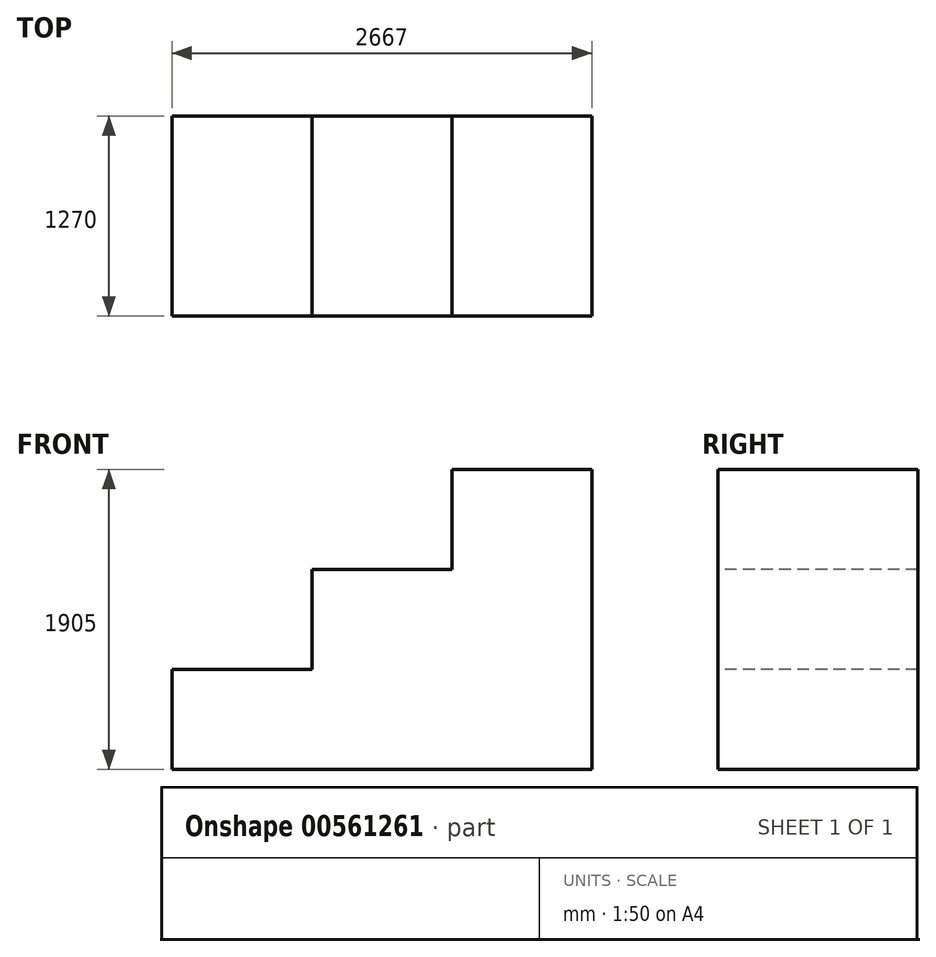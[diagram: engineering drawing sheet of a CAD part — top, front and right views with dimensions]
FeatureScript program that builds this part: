
annotation { "Feature Type Name" : "Feature", "Feature Type Description" : "" }
export const myFeature = defineFeature(function(context is Context, id is Id, definition is map)
    precondition{}
    {
        {
            var Q0;
            Q0=qCreatedBy(makeId("Front.planeOp"),FACE);
            var sketch = newSketch(context, id + "F0", { "sketchPlane" : qUnion([Q0])});
            skLineSegment(sketch, "E0.bottom", {"start": v(-1333.5, 952.5) * mm, "end": v(1333.5, 952.5) * mm});
            skLineSegment(sketch, "E0.top", {"start": v(-1333.5, -952.5) * mm, "end": v(1333.5, -952.5) * mm});
            skLineSegment(sketch, "E0.left", {"start": v(-1333.5, 952.5) * mm, "end": v(-1333.5, -952.5) * mm});
            skLineSegment(sketch, "E0.right", {"start": v(1333.5, 952.5) * mm, "end": v(1333.5, -952.5) * mm});
            skPoint(sketch, "E0.middle", {"position": v(0, 0) * mm});
            skSolve(sketch);
        }
        {
            var Q0;
            Q0 = qSketchRegion(id + "F0", true);
            extrude(context, id + "F1", {"entities" : qUnion([Q0]), "depth" : 1270 * mm, "offsetDistance" : 25.4 * mm});
        }
        {
            var Q0;
            Q0=makeQuery(id+"F1.opExtrude","CAP_FACE",FACE,{"disambiguationData":[OSD([sQuery(id+"F0.wireOp",EDGE,"E0.bottom"),sQuery(id+"F0.wireOp",EDGE,"E0.top"),sQuery(id+"F0.wireOp",EDGE,"E0.left"),sQuery(id+"F0.wireOp",EDGE,"E0.right")])],"isStart":false});
            var sketch = newSketch(context, id + "F2", { "sketchPlane" : qUnion([Q0])});
            skLineSegment(sketch, "E1.bottom", {"start": v(-1333.5, 952.5) * mm, "end": v(-444.5, 952.5) * mm});
            skLineSegment(sketch, "E1.top", {"start": v(-1333.5, 317.5) * mm, "end": v(-444.5, 317.5) * mm});
            skLineSegment(sketch, "E1.left", {"start": v(-1333.5, 952.5) * mm, "end": v(-1333.5, 317.5) * mm});
            skLineSegment(sketch, "E1.right", {"start": v(-444.5, 952.5) * mm, "end": v(-444.5, 317.5) * mm});
            skLineSegment(sketch, "E2.top", {"start": v(-1333.5, -317.5) * mm, "end": v(-444.5, -317.5) * mm});
            skLineSegment(sketch, "E2.left", {"start": v(-1333.5, 317.5) * mm, "end": v(-1333.5, -317.5) * mm});
            skLineSegment(sketch, "E2.right", {"start": v(-444.5, 317.5) * mm, "end": v(-444.5, -317.5) * mm});
            skLineSegment(sketch, "E3.bottom", {"start": v(-444.5, 952.5) * mm, "end": v(444.5, 952.5) * mm});
            skLineSegment(sketch, "E3.top", {"start": v(-444.5, 317.5) * mm, "end": v(444.5, 317.5) * mm});
            skLineSegment(sketch, "E3.right", {"start": v(444.5, 952.5) * mm, "end": v(444.5, 317.5) * mm});
            skSolve(sketch);
        }
        {
            var Q0;
            Q0 = qSketchRegion(id + "F2", true);
            extrude(context, id + "F3", {"entities" : qUnion([Q0]), "operationType" : NewBodyOperationType.REMOVE, "endBound" : BoundingType.THROUGH_ALL, "oppositeDirection" : true, "depth" : 25.4 * mm, "offsetDistance" : 25.4 * mm});
        }
    });
